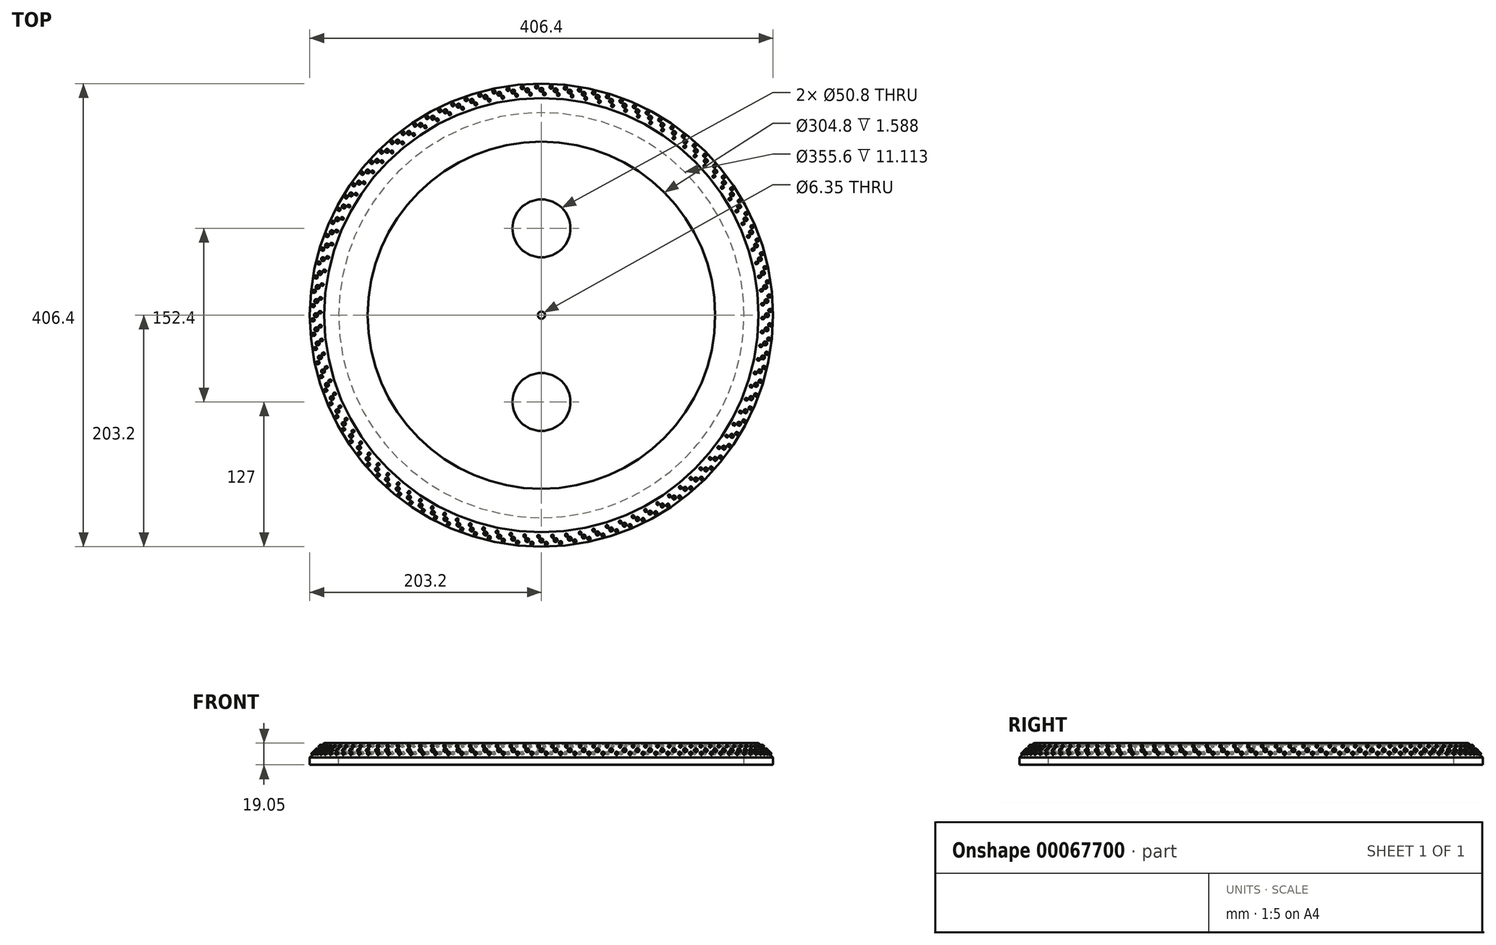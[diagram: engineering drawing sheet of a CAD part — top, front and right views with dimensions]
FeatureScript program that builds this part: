
annotation { "Feature Type Name" : "Feature", "Feature Type Description" : "" }
export const myFeature = defineFeature(function(context is Context, id is Id, definition is map)
    precondition{}
    {
        {
            var Q0;
            Q0=qCreatedBy(makeId("Right.planeOp"),FACE);
            var sketch = newSketch(context, id + "F0", { "sketchPlane" : qUnion([Q0])});
            skLineSegment(sketch, "E0", {"start": v(0, 59.3) * mm, "end": v(0, -57.04) * mm, "construction": true});
            skLineSegment(sketch, "E1", {"start": v(0, 6.35) * mm, "end": v(-152.4, 6.35) * mm});
            skLineSegment(sketch, "E2", {"start": v(-152.4, 6.35) * mm, "end": v(-152.4, 7.94) * mm});
            skLineSegment(sketch, "E3", {"start": v(-152.4, 7.94) * mm, "end": v(-190.5, 7.94) * mm});
            skLineSegment(sketch, "E4", {"start": v(-190.5, 7.94) * mm, "end": v(-203.2, -4.76) * mm});
            skLineSegment(sketch, "E5", {"start": v(-203.2, -4.76) * mm, "end": v(-203.2, -11.11) * mm});
            skLineSegment(sketch, "E6", {"start": v(-203.2, -11.11) * mm, "end": v(-177.8, -11.11) * mm});
            skLineSegment(sketch, "E7", {"start": v(-177.8, 0) * mm, "end": v(0, 0) * mm});
            skLineSegment(sketch, "E8", {"start": v(0, 0) * mm, "end": v(0, 6.35) * mm});
            skLineSegment(sketch, "E9", {"start": v(-177.8, -11.11) * mm, "end": v(-177.8, 0) * mm});
            skSolve(sketch);
        }
        {
            var Q0;
            Q0=makeQuery(id+"F0.imprint","IMPRINT",FACE,{"disambiguationData":[TD([[makeQuery(id+"F0.imprint","IMPRINT",EDGE,{"derivedFrom":sQuery(id+"F0.wireOp",EDGE,"E1")}),1.0]])]});
            var Q1;
            Q1=sQuery(id+"F0.wireOp",EDGE,"E0");
            revolve(context, id + "F1", {"entities" : qUnion([Q0]), "axis" : qUnion([Q1]), "revolveType" : RevolveType.FULL});
        }
        {
            var Q0;
            Q0=sQuery(id+"F0.wireOp",EDGE,"E4");
            cPlane(context, id + "F2", {"entities" : qUnion([Q0]), "cplaneType" : CPlaneType.LINE_ANGLE, "offset" : 152.4 * mm, "angle" : 0 * degree, "width" : 152.4 * mm, "height" : 152.4 * mm});
        }
        {
            var Q0;
            Q0=qCreatedBy(id+"F2.planeOp",FACE);
            cPlane(context, id + "F3", {"entities" : qUnion([Q0]), "cplaneType" : CPlaneType.OFFSET, "offset" : 9.52 * mm, "oppositeDirection" : true, "width" : 152.4 * mm, "height" : 152.4 * mm});
        }
        {
            var Q0;
            Q0=qCreatedBy(id+"F3.planeOp",FACE);
            var sketch = newSketch(context, id + "F4", { "sketchPlane" : qUnion([Q0])});
            skCircle(sketch, "E10", {"center": v(0, -138.62) * mm, "radius": 1.59 * mm});
            skCircle(sketch, "E11", {"center": v(-4.2, -142.43) * mm, "radius": 1.27 * mm});
            skCircle(sketch, "E12", {"center": v(2.54, -133.54) * mm, "radius": 1.02 * mm});
            skSolve(sketch);
        }
        {
            var Q0;
            Q0 = qSketchRegion(id + "F4", true);
            var Q1;
            Q1=makeQuery(id+"F1.opRevolve","SWEPT_FACE",FACE,{"disambiguationData":[OSD([sQuery(id+"F0.wireOp",EDGE,"E4")])]});
            extrude(context, id + "F5", {"entities" : qUnion([Q0]), "operationType" : NewBodyOperationType.ADD, "endBound" : BoundingType.UP_TO_SURFACE, "endBoundEntityFace" : qUnion([Q1]), "depth" : 25.4 * mm});
        }
        {
            var Q0;
            Q0=makeQuery(id+"F5.opExtrude","SWEPT_FACE",FACE,{"disambiguationData":[OSD([sQuery(id+"F4.wireOp",EDGE,"E12")])]});
            var Q1;
            Q1=makeQuery(id+"F5.opExtrude","SWEPT_FACE",FACE,{"disambiguationData":[OSD([sQuery(id+"F4.wireOp",EDGE,"E10")])]});
            var Q2;
            Q2=makeQuery(id+"F5.opExtrude","SWEPT_FACE",FACE,{"disambiguationData":[OSD([sQuery(id+"F4.wireOp",EDGE,"E11")])]});
            var Q3;
            Q3=makeQuery(id+"F5.opExtrude","CAP_FACE",FACE,{"disambiguationData":[OSD([sQuery(id+"F4.wireOp",EDGE,"E10")])],"isStart":true});
            var Q4;
            Q4=makeQuery(id+"F5.opExtrude","CAP_FACE",FACE,{"disambiguationData":[OSD([sQuery(id+"F4.wireOp",EDGE,"E12")])],"isStart":true});
            var Q5;
            Q5=makeQuery(id+"F5.opExtrude","CAP_FACE",FACE,{"disambiguationData":[OSD([sQuery(id+"F4.wireOp",EDGE,"E11")])],"isStart":true});
            var Q6;
            Q6=sQuery(id+"F0.wireOp",EDGE,"E0");
            circularPattern(context, id + "F6", {"faces" : qUnion([Q0, Q1, Q2, Q3, Q4, Q5]), "axis" : qUnion([Q6]), "angle" : 360 * degree, "instanceCount" : 100, "equalSpace" : true, "patternType" : PatternType.FACE});
        }
        {
            var Q0;
            Q0=qCreatedBy(makeId("Right.planeOp"),FACE);
            var sketch = newSketch(context, id + "F7", { "sketchPlane" : qUnion([Q0])});
            skLineSegment(sketch, "E13.0", {"start": v(-192.75, 7.94) * mm, "end": v(-205.45, -4.76) * mm});
            skLineSegment(sketch, "E14", {"start": v(-192.75, 7.94) * mm, "end": v(-192.75, 30.2) * mm});
            skLineSegment(sketch, "E15", {"start": v(-192.75, 30.2) * mm, "end": v(-219.8, 30.2) * mm});
            skLineSegment(sketch, "E16", {"start": v(-219.8, 30.2) * mm, "end": v(-219.8, -4.76) * mm});
            skLineSegment(sketch, "E17", {"start": v(-219.8, -4.76) * mm, "end": v(-205.45, -4.76) * mm});
            skSolve(sketch);
        }
        {
            var Q0;
            Q0=makeQuery(id+"F7.imprint","IMPRINT",FACE,{"disambiguationData":[TD([[makeQuery(id+"F7.imprint","IMPRINT",EDGE,{"derivedFrom":sQuery(id+"F7.wireOp",EDGE,"E13.0")}),-1.0]])]});
            var Q1;
            Q1=sQuery(id+"F0.wireOp",EDGE,"E0");
            revolve(context, id + "F8", {"operationType" : NewBodyOperationType.REMOVE, "entities" : qUnion([Q0]), "axis" : qUnion([Q1]), "revolveType" : RevolveType.FULL, "oppositeDirection" : true});
        }
        {
            var Q0;
            Q0=makeQuery(id+"F1.opRevolve","SWEPT_FACE",FACE,{"disambiguationData":[OSD([sQuery(id+"F0.wireOp",EDGE,"E1")])]});
            var sketch = newSketch(context, id + "F9", { "sketchPlane" : qUnion([Q0])});
            skCircle(sketch, "E18", {"center": v(0, 76.2) * mm, "radius": 25.4 * mm});
            skCircle(sketch, "E19", {"center": v(0, -76.2) * mm, "radius": 25.4 * mm});
            skLineSegment(sketch, "E20", {"start": v(0, 0) * mm, "end": v(52.15, 0) * mm});
            skSolve(sketch);
        }
        {
            var Q0;
            Q0=makeQuery(id+"F9.imprint","IMPRINT",FACE,{"disambiguationData":[TD([[makeQuery(id+"F9.imprint","IMPRINT",EDGE,{"derivedFrom":sQuery(id+"F9.wireOp",EDGE,"E18")}),1.0]])]});
            var Q1;
            Q1=makeQuery(id+"F9.imprint","IMPRINT",FACE,{"disambiguationData":[TD([[makeQuery(id+"F9.imprint","IMPRINT",EDGE,{"derivedFrom":sQuery(id+"F9.wireOp",EDGE,"E19")}),1.0]])]});
            extrude(context, id + "F10", {"entities" : qUnion([Q0, Q1]), "operationType" : NewBodyOperationType.REMOVE, "endBound" : BoundingType.UP_TO_NEXT, "oppositeDirection" : true, "depth" : 25.4 * mm});
        }
        {
            var Q0;
            Q0=makeQuery(id+"F1.opRevolve","SWEPT_FACE",FACE,{"disambiguationData":[OSD([sQuery(id+"F0.wireOp",EDGE,"E1")])]});
            var sketch = newSketch(context, id + "F11", { "sketchPlane" : qUnion([Q0])});
            skCircle(sketch, "E21", {"center": v(0, 0) * mm, "radius": 3.18 * mm});
            skSolve(sketch);
        }
        {
            var Q0;
            Q0=makeQuery(id+"F11.imprint","IMPRINT",FACE,{"disambiguationData":[TD([[makeQuery(id+"F11.imprint","IMPRINT",EDGE,{"derivedFrom":sQuery(id+"F11.wireOp",EDGE,"E21")}),1.0]])]});
            extrude(context, id + "F12", {"entities" : qUnion([Q0]), "operationType" : NewBodyOperationType.REMOVE, "endBound" : BoundingType.UP_TO_NEXT, "oppositeDirection" : true, "depth" : 25.4 * mm});
        }
    });
